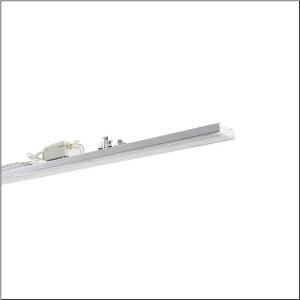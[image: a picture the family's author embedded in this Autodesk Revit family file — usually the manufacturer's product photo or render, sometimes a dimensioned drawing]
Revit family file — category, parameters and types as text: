
# Revit family: licross_11_recessed_mo_51tl19de445g
name_source: partatom
category: Lighting Fixtures
units: mm (PartAtom-declared; Revit-internal decimal feet)

## family parameters
Cut with Voids When Loaded = No
Host = Face
Light Source = No
Part Type = Normal
Room Calculation Point = No
Round Connector Dimension = Use Diameter
Shared = No

## types (1)
- --- (1 x LED, 4900 lm, 29.6 W, 4000K)
    Apparent Load = 30 VA
    CIE Flux Codes = 55 90 98 100 100
    Color Rendering = 80
    Color Temperature = 4000K
    Default Elevation = 1800 mm
    Description = Licross 11 Recessed MO, luminaire insert, of sheet steel, coil coated, white, length: 750mm, width: 66mm, height: 67mm, LED rated luminous flux: 4.910lm, light colour: 840, SDCM (Standard Deviation of Colour Matching)MacAdam ≤ 2 SDCM (initial), control gear: DALI 2, with plug, 5-pole, with phase selection, mains connection: 220..240V, AC, 50/60Hz, rated input power: 30W, internal wiring halogen-free, primary light control with lens, of plastic, primary optical cover: cover, of PMMA, light emission: direct distribution, primary light characteristic: double asymmetric, protection rating (complete): IP40, insulation class (complete): insulation class I (protective earthing), certification: CE, ENEC, VDE, UKCA, protection symbol: D if used in an environment without relevant dust loads with corresponding accessories, impact resistance: IK06, permissible ambient temperature for indoor applications: -25..+35°C, corresponds to IFS (International Featured Standards) requirements for safety and quality in the food industry, reducing of maximum allowable ambient temperature of 5°C with ceiling mounting, LABS conformity tested according to VDMA 24364:2018-05, The light source and the operating device comply with the requirements of the Ecodesign Regulation (EU) 2019/2020 and are replaceable in accordance with this regulation, packaging unit: 1 piece
    Height = 58 mm
    Lamp = 1 x LED
    Lamp Light Flux = 4900 lm
    Lamp Power = 29.6 W
    Lamp count = 1
    Length = 750 mm
    Luminous efficacy = 166 lm/W
    Manufacturer = Siteco
    ModVariant = No
    Model = 51TL19DE445G
    Mounting Place = Ceiling
    Mounting Type = Pendant
    Number of Poles = 1
    OnlyDefault = Yes
    Power Factor = 1
    Product Name = Licross 11 Recessed MO
    Product group = luminaire insert | ceiling pendant
    ProductGroupID = 901
    Protection Class = Protection class I
    Protection Degree = IP 40
    RLX_Detail_Level = 1
    RLX_Emergency_Light_Flux = 0 lm
    RLX_Emergency_Type = 0
    RLX_Emergency_Type_DB = No
    RlxData = <blob elided: 29749 chars, md5=fac051dd>
    Socket = socket
    Standby Power = 0 W
    System Light Flux = 4900 lm
    System Power = 30 W
    Type Comments = factory setting: luminous flux: 100 % | dim-lin: 254 | 378 mA
    Type Image = l_1296930.jpg
    URL = http://relux.com
    VarID = @adj_103779
    Voltage = 0 V
    Weight = 0.00 kg
    Width = 66 mm

## geometry (parser evidence)
native form markers: Blend x4, Sweep x10
no freeform markers — native parametric forms only
